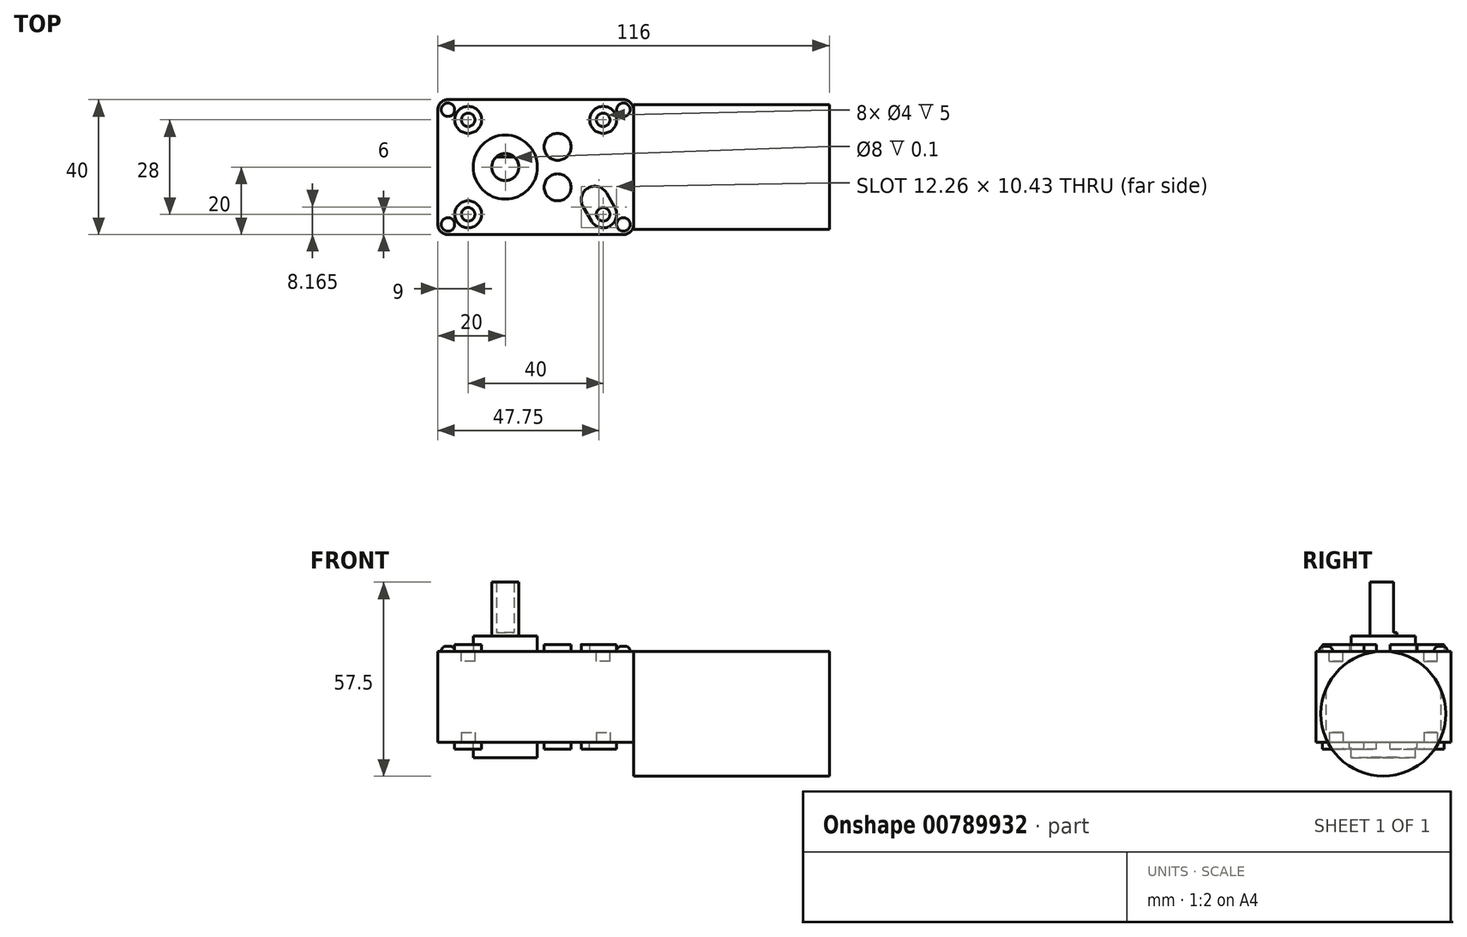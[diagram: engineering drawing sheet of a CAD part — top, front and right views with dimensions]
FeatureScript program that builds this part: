
annotation { "Feature Type Name" : "Feature", "Feature Type Description" : "" }
export const myFeature = defineFeature(function(context is Context, id is Id, definition is map)
    precondition{}
    {
        {
            var Q0;
            Q0=qCreatedBy(makeId("Top.planeOp"),FACE);
            var sketch = newSketch(context, id + "F0", { "sketchPlane" : qUnion([Q0])});
            skLineSegment(sketch, "E0.bottom", {"start": v(35, 20) * mm, "end": v(-17, 20) * mm});
            skLineSegment(sketch, "E0.top", {"start": v(35, -20) * mm, "end": v(-17, -20) * mm});
            skLineSegment(sketch, "E0.left", {"start": v(38, 17) * mm, "end": v(38, -17) * mm});
            skLineSegment(sketch, "E0.right", {"start": v(-20, 17) * mm, "end": v(-20, -17) * mm});
            skPoint(sketch, "E0.middle", {"position": v(9, 0) * mm});
            skPoint(sketch, "E1.visualSharp", {"position": v(-20, 20) * mm});
            skArc(sketch, "E1.filletArc", {"start": v(-17, 20) * mm, "mid": v(-19.12, 19.12) * mm, "end": v(-20, 17) * mm});
            skPoint(sketch, "E2.visualSharp", {"position": v(-20, -20) * mm});
            skArc(sketch, "E2.filletArc", {"start": v(-20, -17) * mm, "mid": v(-19.12, -19.12) * mm, "end": v(-17, -20) * mm});
            skPoint(sketch, "E3.visualSharp", {"position": v(38, -20) * mm});
            skArc(sketch, "E3.filletArc", {"start": v(35, -20) * mm, "mid": v(37.12, -19.12) * mm, "end": v(38, -17) * mm});
            skPoint(sketch, "E4.visualSharp", {"position": v(38, 20) * mm});
            skArc(sketch, "E4.filletArc", {"start": v(38, 17) * mm, "mid": v(37.12, 19.12) * mm, "end": v(35, 20) * mm});
            skSolve(sketch);
        }
        {
            var Q0;
            Q0=qSketchRegion(id+"F0",true);
            extrude(context, id + "F1", {"entities" : qUnion([Q0]), "depth" : 27 * mm});
        }
        {
            var Q0;
            Q0=makeQuery(id+"F1.opExtrude","CAP_FACE",FACE,{"disambiguationData":[OSD([sQuery(id+"F0.wireOp",EDGE,"E0.bottom"),sQuery(id+"F0.wireOp",EDGE,"E0.top"),sQuery(id+"F0.wireOp",EDGE,"E0.left"),sQuery(id+"F0.wireOp",EDGE,"E0.right"),sQuery(id+"F0.wireOp",EDGE,"E1.filletArc"),sQuery(id+"F0.wireOp",EDGE,"E2.filletArc"),sQuery(id+"F0.wireOp",EDGE,"E3.filletArc"),sQuery(id+"F0.wireOp",EDGE,"E4.filletArc")])],"isStart":false});
            var sketch = newSketch(context, id + "F2", { "sketchPlane" : qUnion([Q0])});
            skLineSegment(sketch, "E5.bottom", {"start": v(-11, 14) * mm, "end": v(29, 14) * mm, "construction": true});
            skLineSegment(sketch, "E5.top", {"start": v(-11, -14) * mm, "end": v(29, -14) * mm, "construction": true});
            skLineSegment(sketch, "E5.left", {"start": v(-11, 14) * mm, "end": v(-11, -14) * mm, "construction": true});
            skLineSegment(sketch, "E5.right", {"start": v(29, 14) * mm, "end": v(29, -14) * mm, "construction": true});
            skPoint(sketch, "E5.middle", {"position": v(9, 0) * mm});
            skPoint(sketch, "E5.middle.positionSnap0", {"position": v(9, 20) * mm});
            skPoint(sketch, "E5.centerSnap0", {"position": v(9, 20) * mm});
            skCircle(sketch, "E6", {"center": v(-11, 14) * mm, "radius": 4 * mm});
            skCircle(sketch, "E7", {"center": v(29, 14) * mm, "radius": 4 * mm});
            skCircle(sketch, "E8", {"center": v(-11, -14) * mm, "radius": 4 * mm});
            skArc(sketch, "E9", {"start": v(29.96, -7.67) * mm, "mid": v(24.5, -6.2) * mm, "end": v(23.04, -11.67) * mm});
            skLineSegment(sketch, "E10", {"start": v(23.04, -11.67) * mm, "end": v(25.54, -16) * mm});
            skArc(sketch, "E11.trimOffspring", {"start": v(25.54, -16) * mm, "mid": v(31, -17.46) * mm, "end": v(32.46, -12) * mm});
            skLineSegment(sketch, "E12.trimOffspring", {"start": v(29.96, -7.67) * mm, "end": v(32.46, -12) * mm});
            skLineSegment(sketch, "E13", {"start": v(15.5, 14) * mm, "end": v(15.5, -14) * mm, "construction": true});
            skCircle(sketch, "E14", {"center": v(15.5, 6) * mm, "radius": 4 * mm});
            skCircle(sketch, "E15", {"center": v(15.5, -6) * mm, "radius": 4 * mm});
            skSolve(sketch);
        }
        {
            var Q0;
            Q0=qSketchRegion(id+"F2",true);
            extrude(context, id + "F3", {"entities" : qUnion([Q0]), "operationType" : NewBodyOperationType.ADD, "depth" : 2 * mm});
        }
        {
            var Q0;
            Q0=qSketchRegion(id+"F2",true);
            extrude(context, id + "F4", {"entities" : qUnion([Q0]), "operationType" : NewBodyOperationType.ADD, "oppositeDirection" : true, "depth" : 29 * mm});
        }
        {
            var Q0;
            Q0=makeQuery(id+"F1.opExtrude","CAP_FACE",FACE,{"disambiguationData":[OSD([sQuery(id+"F0.wireOp",EDGE,"E0.bottom"),sQuery(id+"F0.wireOp",EDGE,"E0.top"),sQuery(id+"F0.wireOp",EDGE,"E0.left"),sQuery(id+"F0.wireOp",EDGE,"E0.right"),sQuery(id+"F0.wireOp",EDGE,"E1.filletArc"),sQuery(id+"F0.wireOp",EDGE,"E2.filletArc"),sQuery(id+"F0.wireOp",EDGE,"E3.filletArc"),sQuery(id+"F0.wireOp",EDGE,"E4.filletArc")])],"isStart":false});
            var sketch = newSketch(context, id + "F5", { "sketchPlane" : qUnion([Q0])});
            skCircle(sketch, "E16", {"center": v(0, 0) * mm, "radius": 9.5 * mm});
            skSolve(sketch);
        }
        {
            var Q0;
            Q0=qSketchRegion(id+"F5",true);
            extrude(context, id + "F6", {"entities" : qUnion([Q0]), "operationType" : NewBodyOperationType.ADD, "depth" : 4.5 * mm});
        }
        {
            var Q0;
            Q0=qSketchRegion(id+"F5",true);
            extrude(context, id + "F7", {"entities" : qUnion([Q0]), "operationType" : NewBodyOperationType.ADD, "oppositeDirection" : true, "depth" : 31.5 * mm});
        }
        {
            var Q0;
            Q0=makeQuery(id+"F6.opExtrude","CAP_FACE",FACE,{"disambiguationData":[OSD([sQuery(id+"F5.wireOp",EDGE,"E16")])],"isStart":false});
            var sketch = newSketch(context, id + "F8", { "sketchPlane" : qUnion([Q0])});
            skCircle(sketch, "E17", {"center": v(0, 0) * mm, "radius": 4 * mm});
            skSolve(sketch);
        }
        {
            var Q0;
            Q0=qSketchRegion(id+"F8",true);
            extrude(context, id + "F9", {"entities" : qUnion([Q0]), "operationType" : NewBodyOperationType.ADD, "depth" : 1 * mm});
        }
        {
            var Q0;
            Q0=makeQuery(id+"F9.opExtrude","CAP_FACE",FACE,{"disambiguationData":[OSD([sQuery(id+"F8.wireOp",EDGE,"E17")])],"isStart":false});
            var sketch = newSketch(context, id + "F10", { "sketchPlane" : qUnion([Q0])});
            skArc(sketch, "E18", {"start": v(-2.65, 3) * mm, "mid": v(0, -4) * mm, "end": v(2.65, 3) * mm});
            skLineSegment(sketch, "E19", {"start": v(-2.65, 3) * mm, "end": v(2.65, 3) * mm});
            skSolve(sketch);
        }
        {
            var Q0;
            Q0=qSketchRegion(id+"F10",true);
            extrude(context, id + "F11", {"entities" : qUnion([Q0]), "operationType" : NewBodyOperationType.ADD, "depth" : 15 * mm});
        }
        {
            var Q0;
            Q0=makeQuery(id+"F7.opExtrude","CAP_FACE",FACE,{"disambiguationData":[OSD([sQuery(id+"F5.wireOp",EDGE,"E16")])],"isStart":false});
            var sketch = newSketch(context, id + "F12", { "sketchPlane" : qUnion([Q0])});
            skCircle(sketch, "E20", {"center": v(0, 0) * mm, "radius": 4 * mm});
            skSolve(sketch);
        }
        {
            var Q0;
            Q0=qSketchRegion(id+"F12",true);
            extrude(context, id + "F13", {"entities" : qUnion([Q0]), "operationType" : NewBodyOperationType.REMOVE, "oppositeDirection" : true, "depth" : 0.1 * mm});
        }
        {
            var Q0;
            Q0=makeQuery(id+"F1.opExtrude","SWEPT_FACE",FACE,{"disambiguationData":[OSD([sQuery(id+"F0.wireOp",EDGE,"E0.left")])]});
            var sketch = newSketch(context, id + "F14", { "sketchPlane" : qUnion([Q0])});
            skCircle(sketch, "E21", {"center": v(0, 8.5) * mm, "radius": 18.5 * mm});
            skSolve(sketch);
        }
        {
            var Q0;
            Q0=qSketchRegion(id+"F14",true);
            extrude(context, id + "F15", {"entities" : qUnion([Q0]), "operationType" : NewBodyOperationType.ADD, "depth" : 58 * mm});
        }
        {
            var Q0;
            Q0=makeQuery(id+"F1.opExtrude","CAP_FACE",FACE,{"disambiguationData":[OSD([sQuery(id+"F0.wireOp",EDGE,"E0.bottom"),sQuery(id+"F0.wireOp",EDGE,"E0.top"),sQuery(id+"F0.wireOp",EDGE,"E0.left"),sQuery(id+"F0.wireOp",EDGE,"E0.right"),sQuery(id+"F0.wireOp",EDGE,"E1.filletArc"),sQuery(id+"F0.wireOp",EDGE,"E2.filletArc"),sQuery(id+"F0.wireOp",EDGE,"E3.filletArc"),sQuery(id+"F0.wireOp",EDGE,"E4.filletArc")])],"isStart":false});
            var sketch = newSketch(context, id + "F16", { "sketchPlane" : qUnion([Q0])});
            skCircle(sketch, "E22", {"center": v(-17, 17) * mm, "radius": 2 * mm});
            skCircle(sketch, "E23", {"center": v(35, 17) * mm, "radius": 2 * mm});
            skCircle(sketch, "E24", {"center": v(35, -17) * mm, "radius": 2 * mm});
            skCircle(sketch, "E25", {"center": v(-17, -17) * mm, "radius": 2 * mm});
            skSolve(sketch);
        }
        {
            var Q0;
            Q0=qSketchRegion(id+"F16",true);
            extrude(context, id + "F17", {"entities" : qUnion([Q0]), "operationType" : NewBodyOperationType.ADD, "depth" : 1.5 * mm});
        }
        {
            var Q0;
            Q0=makeQuery(id+"F17.opExtrude","CAP_EDGE",EDGE,{"disambiguationData":[OSD([sQuery(id+"F16.wireOp",EDGE,"E22")])],"isStart":false});
            var Q1;
            Q1=makeQuery(id+"F17.opExtrude","CAP_EDGE",EDGE,{"disambiguationData":[OSD([sQuery(id+"F16.wireOp",EDGE,"E25")])],"isStart":false});
            var Q2;
            Q2=makeQuery(id+"F17.opExtrude","CAP_EDGE",EDGE,{"disambiguationData":[OSD([sQuery(id+"F16.wireOp",EDGE,"E24")])],"isStart":false});
            var Q3;
            Q3=makeQuery(id+"F17.opExtrude","CAP_EDGE",EDGE,{"disambiguationData":[OSD([sQuery(id+"F16.wireOp",EDGE,"E23")])],"isStart":false});
            fillet(context, id + "F18", {"entities" : qUnion([Q0, Q1, Q2, Q3]), "radius" : 1.5 * mm, "tangentPropagation" : true, "allowEdgeOverflow" : false});
        }
        {
            var Q0;
            Q0=makeQuery(id+"F3.opExtrude","CAP_FACE",FACE,{"disambiguationData":[OSD([sQuery(id+"F2.wireOp",EDGE,"E6")])],"isStart":false});
            var sketch = newSketch(context, id + "F19", { "sketchPlane" : qUnion([Q0])});
            skCircle(sketch, "E26", {"center": v(-11, 14) * mm, "radius": 2 * mm});
            skCircle(sketch, "E27", {"center": v(-11, -14) * mm, "radius": 2 * mm});
            skCircle(sketch, "E28", {"center": v(29, -14) * mm, "radius": 2 * mm});
            skCircle(sketch, "E29", {"center": v(29, 14) * mm, "radius": 2 * mm});
            skSolve(sketch);
        }
        {
            var Q0;
            Q0=qSketchRegion(id+"F19",true);
            extrude(context, id + "F20", {"entities" : qUnion([Q0]), "operationType" : NewBodyOperationType.REMOVE, "oppositeDirection" : true, "depth" : 5 * mm});
        }
        {
            var Q0;
            Q0=makeQuery(id+"F4.opExtrude","CAP_FACE",FACE,{"disambiguationData":[OSD([sQuery(id+"F2.wireOp",EDGE,"E9"),sQuery(id+"F2.wireOp",EDGE,"E10"),sQuery(id+"F2.wireOp",EDGE,"E11.trimOffspring"),sQuery(id+"F2.wireOp",EDGE,"E12.trimOffspring")])],"isStart":false});
            var sketch = newSketch(context, id + "F21", { "sketchPlane" : qUnion([Q0])});
            skCircle(sketch, "E30", {"center": v(29, 14) * mm, "radius": 2 * mm});
            skCircle(sketch, "E31", {"center": v(29, -14) * mm, "radius": 2 * mm});
            skCircle(sketch, "E32", {"center": v(-11, -14) * mm, "radius": 2 * mm});
            skCircle(sketch, "E33", {"center": v(-11, 14) * mm, "radius": 2 * mm});
            skSolve(sketch);
        }
        {
            var Q0;
            Q0=qSketchRegion(id+"F21",true);
            extrude(context, id + "F22", {"entities" : qUnion([Q0]), "operationType" : NewBodyOperationType.REMOVE, "oppositeDirection" : true, "depth" : 5 * mm});
        }
    });
